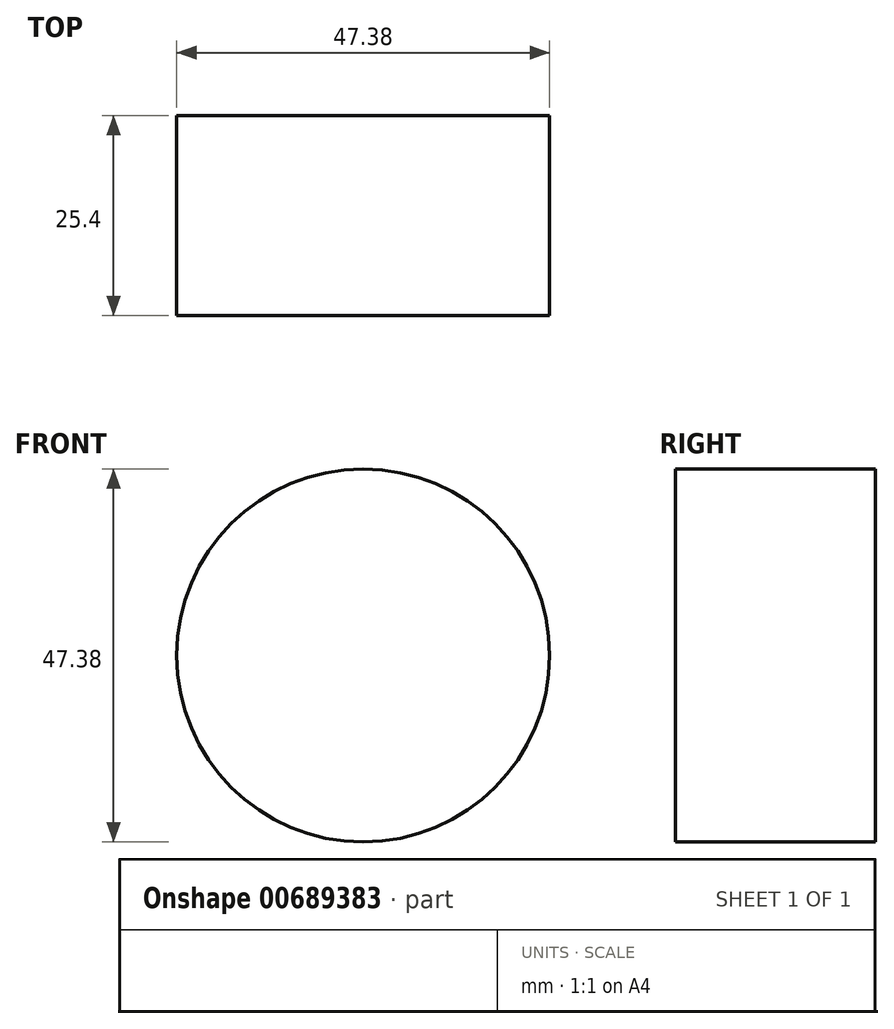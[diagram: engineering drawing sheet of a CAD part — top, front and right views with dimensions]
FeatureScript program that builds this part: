
annotation { "Feature Type Name" : "Feature", "Feature Type Description" : "" }
export const myFeature = defineFeature(function(context is Context, id is Id, definition is map)
    precondition{}
    {
        {
            var Q0;
            Q0=qCreatedBy(makeId("Front.planeOp"),FACE);
            var sketch = newSketch(context, id + "F0", { "sketchPlane" : qUnion([Q0])});
            skCircle(sketch, "E0", {"center": v(0, 0) * mm, "radius": 23.69 * mm});
            skSolve(sketch);
        }
        {
            var Q0;
            Q0 = qSketchRegion(id + "F0", true);
            extrude(context, id + "F1", {"entities" : qUnion([Q0]), "depth" : 25.4 * mm, "offsetDistance" : 25.4 * mm});
        }
    });
